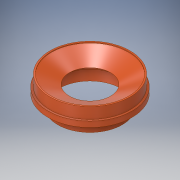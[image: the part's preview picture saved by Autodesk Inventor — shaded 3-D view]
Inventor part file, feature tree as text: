
AUTODESK INVENTOR PART (.ipt)
format: ipt  version: 2017 SP1 (Build 210196100, 196)  size: 183,808 bytes
history: native  units: in
note: dims shown in document units (in); Inventor stores cm internally (conversion verified against a paired STEP export)
features: revolve x1, sketch x1
ambient origin geometry x8: Origin, YZ Plane, XZ Plane, XY Plane, X Axis, Y Axis, Z Axis, Center Point
bodies: Solid1 (feature_tree)
feature tree (2):
  revolve  "Revolution1"  [1 undecoded]
  sketch  "Sketch1"  dims[d0=1.13in d1=3.75in d2=0.175in d5=1.0in d6=1.0in d7=90.0deg d8=0.5in d9=15.0deg d12=1.25in d13=0.25in d16=0.5in d17=0.5in d18=0.5in d19=2.5in d20=0.5in d22=0.375in d23=0.25in d25=0.234in d27=0.125in d28=0.25in d29=1.0in d30=4.25in d31=0.25in d33=0.8014in d34=15.0deg d35=0.125in d36=1.0in d37=90.0deg d38=0.125in d39=0.0583in d40=0.1718in]
note: 1 required parameter value undecoded (feature->parameter linkage not recoverable at this tier; creation-order binding heuristic only, values carry confidence <= 0.55)
